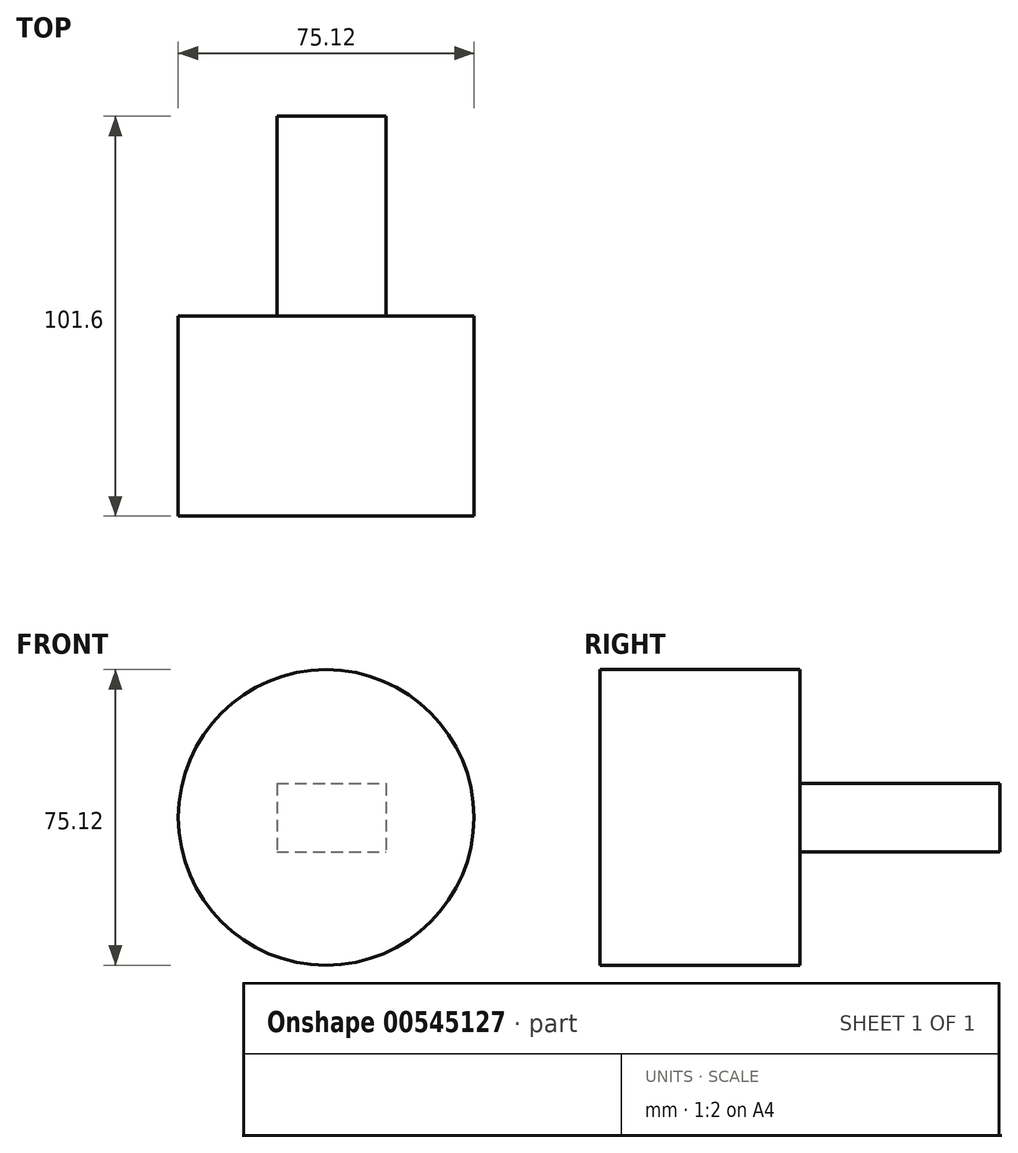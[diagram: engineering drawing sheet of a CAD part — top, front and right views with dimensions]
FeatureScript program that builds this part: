
annotation { "Feature Type Name" : "Feature", "Feature Type Description" : "" }
export const myFeature = defineFeature(function(context is Context, id is Id, definition is map)
    precondition{}
    {
        {
            var Q0;
            Q0=qCreatedBy(makeId("Front.planeOp"),FACE);
            var sketch = newSketch(context, id + "F0", { "sketchPlane" : qUnion([Q0])});
            skCircle(sketch, "E0", {"center": v(0, 0) * mm, "radius": 37.56 * mm});
            skSolve(sketch);
        }
        {
            var Q0;
            Q0=makeQuery(id+"F0.imprint","IMPRINT",FACE,{"disambiguationData":[TD([[makeQuery(id+"F0.imprint","IMPRINT",EDGE,{"derivedFrom":sQuery(id+"F0.wireOp",EDGE,"E0")}),1.0]])]});
            extrude(context, id + "F1", {"entities" : qUnion([Q0]), "depth" : 50.8 * mm, "offsetDistance" : 25.4 * mm});
        }
        {
            var Q0;
            Q0=qCreatedBy(makeId("Front.planeOp"),FACE);
            var sketch = newSketch(context, id + "F2", { "sketchPlane" : qUnion([Q0])});
            skLineSegment(sketch, "E1.bottom", {"start": v(-12.53, 8.6) * mm, "end": v(15.24, 8.6) * mm});
            skLineSegment(sketch, "E1.top", {"start": v(-12.53, -8.79) * mm, "end": v(15.24, -8.79) * mm});
            skLineSegment(sketch, "E1.left", {"start": v(-12.53, 8.6) * mm, "end": v(-12.53, -8.79) * mm});
            skLineSegment(sketch, "E1.right", {"start": v(15.24, 8.6) * mm, "end": v(15.24, -8.79) * mm});
            skSolve(sketch);
        }
        {
            var Q0;
            Q0 = qSketchRegion(id + "F2", true);
            extrude(context, id + "F3", {"entities" : qUnion([Q0]), "operationType" : NewBodyOperationType.ADD, "oppositeDirection" : true, "depth" : 50.8 * mm, "offsetDistance" : 25.4 * mm});
        }
    });
